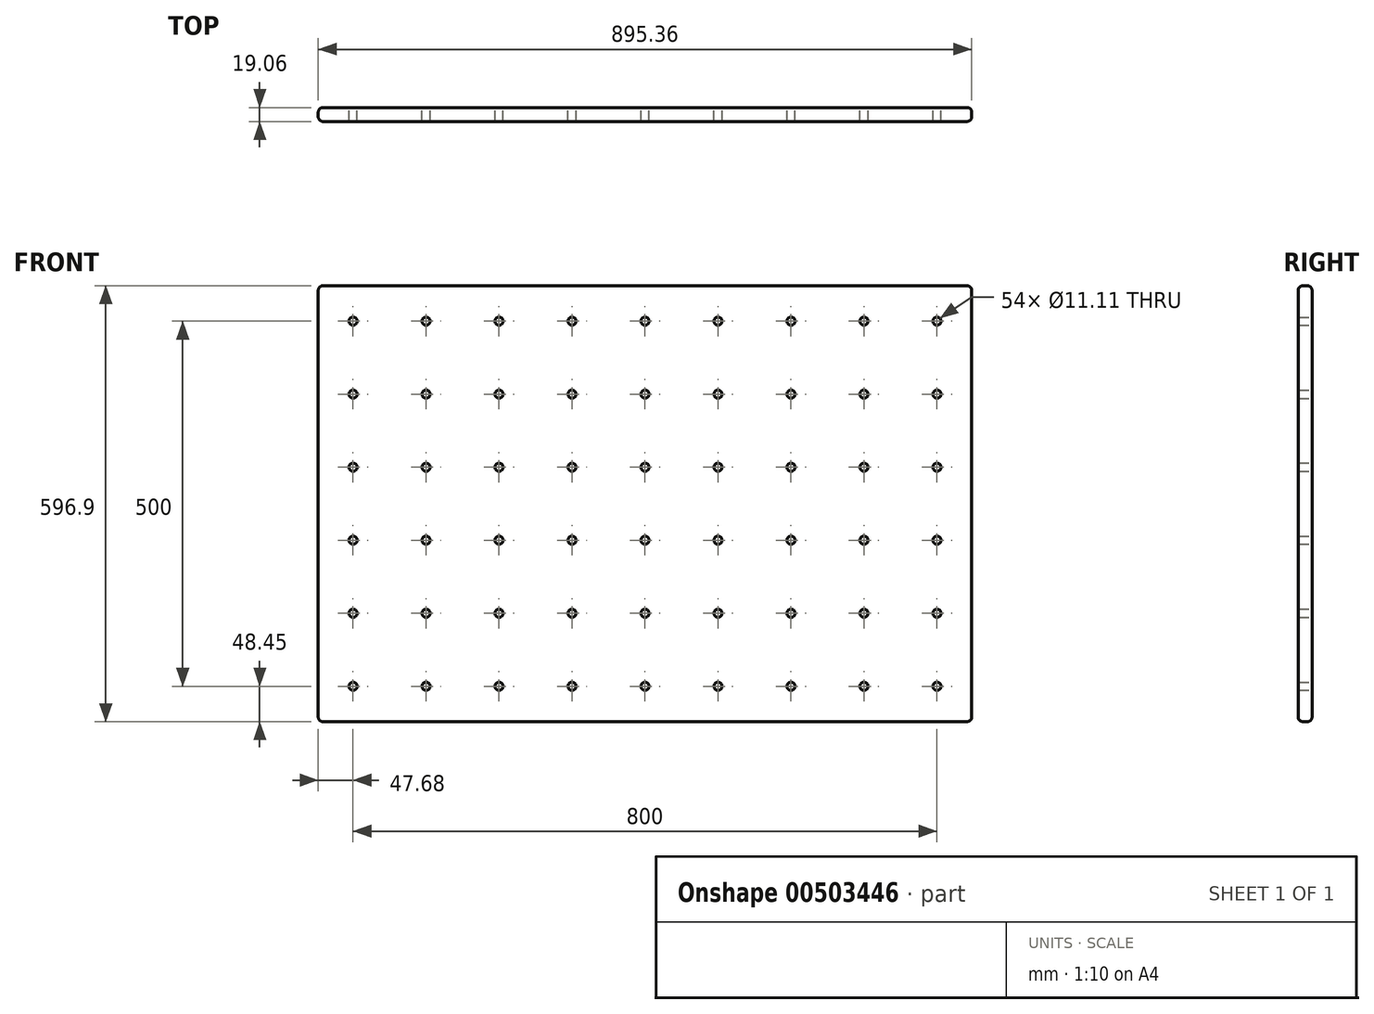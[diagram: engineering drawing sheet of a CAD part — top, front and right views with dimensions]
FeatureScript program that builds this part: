
annotation { "Feature Type Name" : "Feature", "Feature Type Description" : "" }
export const myFeature = defineFeature(function(context is Context, id is Id, definition is map)
    precondition{}
    {
        {
            var Q0;
            Q0=qCreatedBy(makeId("Front.planeOp"),FACE);
            var sketch = newSketch(context, id + "F0", { "sketchPlane" : qUnion([Q0])});
            skLineSegment(sketch, "E0.bottom", {"start": v(-447.68, 298.45) * mm, "end": v(447.68, 298.45) * mm});
            skLineSegment(sketch, "E0.top", {"start": v(-447.68, -298.45) * mm, "end": v(447.67, -298.45) * mm});
            skLineSegment(sketch, "E0.left", {"start": v(-447.68, 298.45) * mm, "end": v(-447.68, -298.45) * mm});
            skLineSegment(sketch, "E0.right", {"start": v(447.68, 298.45) * mm, "end": v(447.67, -298.45) * mm});
            skCircle(sketch, "E1", {"center": v(400, -250) * mm, "radius": 5.56 * mm});
            skCircle(sketch, "E2.0.1.0", {"center": v(400, -150) * mm, "radius": 5.56 * mm});
            skCircle(sketch, "E2.0.2.0", {"center": v(400, -50) * mm, "radius": 5.56 * mm});
            skCircle(sketch, "E2.0.3.0", {"center": v(400, 50) * mm, "radius": 5.56 * mm});
            skCircle(sketch, "E2.0.4.0", {"center": v(400, 150) * mm, "radius": 5.56 * mm});
            skCircle(sketch, "E2.0.5.0", {"center": v(400, 250) * mm, "radius": 5.56 * mm});
            skCircle(sketch, "E2.1.0.0", {"center": v(300, -250) * mm, "radius": 5.56 * mm});
            skCircle(sketch, "E2.1.1.0", {"center": v(300, -150) * mm, "radius": 5.56 * mm});
            skCircle(sketch, "E2.1.2.0", {"center": v(300, -50) * mm, "radius": 5.56 * mm});
            skCircle(sketch, "E2.1.3.0", {"center": v(300, 50) * mm, "radius": 5.56 * mm});
            skCircle(sketch, "E2.1.4.0", {"center": v(300, 150) * mm, "radius": 5.56 * mm});
            skCircle(sketch, "E2.1.5.0", {"center": v(300, 250) * mm, "radius": 5.56 * mm});
            skCircle(sketch, "E2.2.0.0", {"center": v(200, -250) * mm, "radius": 5.56 * mm});
            skCircle(sketch, "E2.2.1.0", {"center": v(200, -150) * mm, "radius": 5.56 * mm});
            skCircle(sketch, "E2.2.2.0", {"center": v(200, -50) * mm, "radius": 5.56 * mm});
            skCircle(sketch, "E2.2.3.0", {"center": v(200, 50) * mm, "radius": 5.56 * mm});
            skCircle(sketch, "E2.2.4.0", {"center": v(200, 150) * mm, "radius": 5.56 * mm});
            skCircle(sketch, "E2.2.5.0", {"center": v(200, 250) * mm, "radius": 5.56 * mm});
            skCircle(sketch, "E2.3.0.0", {"center": v(100, -250) * mm, "radius": 5.56 * mm});
            skCircle(sketch, "E2.3.1.0", {"center": v(100, -150) * mm, "radius": 5.56 * mm});
            skCircle(sketch, "E2.3.2.0", {"center": v(100, -50) * mm, "radius": 5.56 * mm});
            skCircle(sketch, "E2.3.3.0", {"center": v(100, 50) * mm, "radius": 5.56 * mm});
            skCircle(sketch, "E2.3.4.0", {"center": v(100, 150) * mm, "radius": 5.56 * mm});
            skCircle(sketch, "E2.3.5.0", {"center": v(100, 250) * mm, "radius": 5.56 * mm});
            skCircle(sketch, "E2.4.0.0", {"center": v(0, -250) * mm, "radius": 5.56 * mm});
            skCircle(sketch, "E2.4.1.0", {"center": v(0, -150) * mm, "radius": 5.56 * mm});
            skCircle(sketch, "E2.4.2.0", {"center": v(0, -50) * mm, "radius": 5.56 * mm});
            skCircle(sketch, "E2.4.3.0", {"center": v(0, 50) * mm, "radius": 5.56 * mm});
            skCircle(sketch, "E2.4.4.0", {"center": v(0, 150) * mm, "radius": 5.56 * mm});
            skCircle(sketch, "E2.4.5.0", {"center": v(0, 250) * mm, "radius": 5.56 * mm});
            skCircle(sketch, "E2.5.0.0", {"center": v(-100, -250) * mm, "radius": 5.56 * mm});
            skCircle(sketch, "E2.5.1.0", {"center": v(-100, -150) * mm, "radius": 5.56 * mm});
            skCircle(sketch, "E2.5.2.0", {"center": v(-100, -50) * mm, "radius": 5.56 * mm});
            skCircle(sketch, "E2.5.3.0", {"center": v(-100, 50) * mm, "radius": 5.56 * mm});
            skCircle(sketch, "E2.5.4.0", {"center": v(-100, 150) * mm, "radius": 5.56 * mm});
            skCircle(sketch, "E2.5.5.0", {"center": v(-100, 250) * mm, "radius": 5.56 * mm});
            skCircle(sketch, "E2.6.0.0", {"center": v(-200, -250) * mm, "radius": 5.56 * mm});
            skCircle(sketch, "E2.6.1.0", {"center": v(-200, -150) * mm, "radius": 5.56 * mm});
            skCircle(sketch, "E2.6.2.0", {"center": v(-200, -50) * mm, "radius": 5.56 * mm});
            skCircle(sketch, "E2.6.3.0", {"center": v(-200, 50) * mm, "radius": 5.56 * mm});
            skCircle(sketch, "E2.6.4.0", {"center": v(-200, 150) * mm, "radius": 5.56 * mm});
            skCircle(sketch, "E2.6.5.0", {"center": v(-200, 250) * mm, "radius": 5.56 * mm});
            skCircle(sketch, "E2.7.0.0", {"center": v(-300, -250) * mm, "radius": 5.56 * mm});
            skCircle(sketch, "E2.7.1.0", {"center": v(-300, -150) * mm, "radius": 5.56 * mm});
            skCircle(sketch, "E2.7.2.0", {"center": v(-300, -50) * mm, "radius": 5.56 * mm});
            skCircle(sketch, "E2.7.3.0", {"center": v(-300, 50) * mm, "radius": 5.56 * mm});
            skCircle(sketch, "E2.7.4.0", {"center": v(-300, 150) * mm, "radius": 5.56 * mm});
            skCircle(sketch, "E2.7.5.0", {"center": v(-300, 250) * mm, "radius": 5.56 * mm});
            skCircle(sketch, "E2.8.0.0", {"center": v(-400, -250) * mm, "radius": 5.56 * mm});
            skCircle(sketch, "E2.8.1.0", {"center": v(-400, -150) * mm, "radius": 5.56 * mm});
            skCircle(sketch, "E2.8.2.0", {"center": v(-400, -50) * mm, "radius": 5.56 * mm});
            skCircle(sketch, "E2.8.3.0", {"center": v(-400, 50) * mm, "radius": 5.56 * mm});
            skCircle(sketch, "E2.8.4.0", {"center": v(-400, 150) * mm, "radius": 5.56 * mm});
            skCircle(sketch, "E2.8.5.0", {"center": v(-400, 250) * mm, "radius": 5.56 * mm});
            skLineSegment(sketch, "E2.direction1", {"start": v(400, -250) * mm, "end": v(300, -250) * mm, "construction": true});
            skLineSegment(sketch, "E2.direction2", {"start": v(400, -250) * mm, "end": v(400, -150) * mm, "construction": true});
            skSolve(sketch);
        }
        {
            var Q0;
            Q0=makeQuery(id+"F0.imprint","IMPRINT",FACE,{"disambiguationData":[TD([[makeQuery(id+"F0.imprint","IMPRINT",EDGE,{"derivedFrom":sQuery(id+"F0.wireOp",EDGE,"E0.bottom")}),-1.0]])]});
            extrude(context, id + "F1", {"entities" : qUnion([Q0]), "depth" : 19.05 * mm, "symmetric" : true});
        }
        {
            var Q0;
            Q0=makeQuery(id+"F1.opExtrude","SWEPT_EDGE",EDGE,{"disambiguationData":[OSD([sQuery(id+"F0.wireOp",EDGE,"E0.bottom"),sQuery(id+"F0.wireOp",EDGE,"E0.left")])]});
            var Q1;
            Q1=makeQuery(id+"F1.opExtrude","CAP_EDGE",EDGE,{"disambiguationData":[OSD([sQuery(id+"F0.wireOp",EDGE,"E0.bottom")])],"isStart":true});
            var Q2;
            Q2=makeQuery(id+"F1.opExtrude","CAP_EDGE",EDGE,{"disambiguationData":[OSD([sQuery(id+"F0.wireOp",EDGE,"E0.left")])],"isStart":true});
            var Q3;
            Q3=makeQuery(id+"F1.opExtrude","CAP_EDGE",EDGE,{"disambiguationData":[OSD([sQuery(id+"F0.wireOp",EDGE,"E0.left")])],"isStart":false});
            var Q4;
            Q4=makeQuery(id+"F1.opExtrude","SWEPT_EDGE",EDGE,{"disambiguationData":[OSD([sQuery(id+"F0.wireOp",EDGE,"E0.bottom"),sQuery(id+"F0.wireOp",EDGE,"E0.right")])]});
            var Q5;
            Q5=makeQuery(id+"F1.opExtrude","CAP_EDGE",EDGE,{"disambiguationData":[OSD([sQuery(id+"F0.wireOp",EDGE,"E0.bottom")])],"isStart":false});
            var Q6;
            Q6=makeQuery(id+"F1.opExtrude","CAP_EDGE",EDGE,{"disambiguationData":[OSD([sQuery(id+"F0.wireOp",EDGE,"E0.right")])],"isStart":false});
            var Q7;
            Q7=makeQuery(id+"F1.opExtrude","CAP_EDGE",EDGE,{"disambiguationData":[OSD([sQuery(id+"F0.wireOp",EDGE,"E0.top")])],"isStart":false});
            var Q8;
            Q8=makeQuery(id+"F1.opExtrude","SWEPT_EDGE",EDGE,{"disambiguationData":[OSD([sQuery(id+"F0.wireOp",EDGE,"E0.top"),sQuery(id+"F0.wireOp",EDGE,"E0.left")])]});
            var Q9;
            Q9=makeQuery(id+"F1.opExtrude","CAP_EDGE",EDGE,{"disambiguationData":[OSD([sQuery(id+"F0.wireOp",EDGE,"E0.top")])],"isStart":true});
            var Q10;
            Q10=makeQuery(id+"F1.opExtrude","SWEPT_EDGE",EDGE,{"disambiguationData":[OSD([sQuery(id+"F0.wireOp",EDGE,"E0.top"),sQuery(id+"F0.wireOp",EDGE,"E0.right")])]});
            var Q11;
            Q11=makeQuery(id+"F1.opExtrude","CAP_EDGE",EDGE,{"disambiguationData":[OSD([sQuery(id+"F0.wireOp",EDGE,"E0.right")])],"isStart":true});
            fillet(context, id + "F2", {"entities" : qUnion([Q0, Q1, Q2, Q3, Q4, Q5, Q6, Q7, Q8, Q9, Q10, Q11]), "radius" : 6.35 * mm, "tangentPropagation" : true, "allowEdgeOverflow" : false});
        }
        {
            var Q0;
            Q0=makeQuery(id+"F1.opExtrude","CAP_FACE",FACE,{"disambiguationData":[OSD([sQuery(id+"F0.wireOp",EDGE,"E0.bottom"),sQuery(id+"F0.wireOp",EDGE,"E0.top"),sQuery(id+"F0.wireOp",EDGE,"E0.left"),sQuery(id+"F0.wireOp",EDGE,"E0.right"),sQuery(id+"F0.wireOp",EDGE,"E1"),sQuery(id+"F0.wireOp",EDGE,"E2.0.1.0"),sQuery(id+"F0.wireOp",EDGE,"E2.0.2.0"),sQuery(id+"F0.wireOp",EDGE,"E2.0.3.0"),sQuery(id+"F0.wireOp",EDGE,"E2.0.4.0"),sQuery(id+"F0.wireOp",EDGE,"E2.0.5.0"),sQuery(id+"F0.wireOp",EDGE,"E2.1.0.0"),sQuery(id+"F0.wireOp",EDGE,"E2.1.1.0"),sQuery(id+"F0.wireOp",EDGE,"E2.1.2.0"),sQuery(id+"F0.wireOp",EDGE,"E2.1.3.0"),sQuery(id+"F0.wireOp",EDGE,"E2.1.4.0"),sQuery(id+"F0.wireOp",EDGE,"E2.1.5.0"),sQuery(id+"F0.wireOp",EDGE,"E2.2.0.0"),sQuery(id+"F0.wireOp",EDGE,"E2.2.1.0"),sQuery(id+"F0.wireOp",EDGE,"E2.2.2.0"),sQuery(id+"F0.wireOp",EDGE,"E2.2.3.0"),sQuery(id+"F0.wireOp",EDGE,"E2.2.4.0"),sQuery(id+"F0.wireOp",EDGE,"E2.2.5.0"),sQuery(id+"F0.wireOp",EDGE,"E2.3.0.0"),sQuery(id+"F0.wireOp",EDGE,"E2.3.1.0"),sQuery(id+"F0.wireOp",EDGE,"E2.3.2.0"),sQuery(id+"F0.wireOp",EDGE,"E2.3.3.0"),sQuery(id+"F0.wireOp",EDGE,"E2.3.4.0"),sQuery(id+"F0.wireOp",EDGE,"E2.3.5.0"),sQuery(id+"F0.wireOp",EDGE,"E2.4.0.0"),sQuery(id+"F0.wireOp",EDGE,"E2.4.1.0"),sQuery(id+"F0.wireOp",EDGE,"E2.4.2.0"),sQuery(id+"F0.wireOp",EDGE,"E2.4.3.0"),sQuery(id+"F0.wireOp",EDGE,"E2.4.4.0"),sQuery(id+"F0.wireOp",EDGE,"E2.4.5.0"),sQuery(id+"F0.wireOp",EDGE,"E2.5.0.0"),sQuery(id+"F0.wireOp",EDGE,"E2.5.1.0"),sQuery(id+"F0.wireOp",EDGE,"E2.5.2.0"),sQuery(id+"F0.wireOp",EDGE,"E2.5.3.0"),sQuery(id+"F0.wireOp",EDGE,"E2.5.4.0"),sQuery(id+"F0.wireOp",EDGE,"E2.5.5.0"),sQuery(id+"F0.wireOp",EDGE,"E2.6.0.0"),sQuery(id+"F0.wireOp",EDGE,"E2.6.1.0"),sQuery(id+"F0.wireOp",EDGE,"E2.6.2.0"),sQuery(id+"F0.wireOp",EDGE,"E2.6.3.0"),sQuery(id+"F0.wireOp",EDGE,"E2.6.4.0"),sQuery(id+"F0.wireOp",EDGE,"E2.6.5.0"),sQuery(id+"F0.wireOp",EDGE,"E2.7.0.0"),sQuery(id+"F0.wireOp",EDGE,"E2.7.1.0"),sQuery(id+"F0.wireOp",EDGE,"E2.7.2.0"),sQuery(id+"F0.wireOp",EDGE,"E2.7.3.0"),sQuery(id+"F0.wireOp",EDGE,"E2.7.4.0"),sQuery(id+"F0.wireOp",EDGE,"E2.7.5.0"),sQuery(id+"F0.wireOp",EDGE,"E2.8.0.0"),sQuery(id+"F0.wireOp",EDGE,"E2.8.1.0"),sQuery(id+"F0.wireOp",EDGE,"E2.8.2.0"),sQuery(id+"F0.wireOp",EDGE,"E2.8.3.0"),sQuery(id+"F0.wireOp",EDGE,"E2.8.4.0"),sQuery(id+"F0.wireOp",EDGE,"E2.8.5.0")])],"isStart":false});
            var sketch = newSketch(context, id + "F3", { "sketchPlane" : qUnion([Q0])});
            skLineSegment(sketch, "E3", {"start": v(-400.05, 200) * mm, "end": v(0, 200) * mm});
            skLineSegment(sketch, "E4.MirrorCS", {"start": v(400.05, 200) * mm, "end": v(0, 200) * mm});
            skLineSegment(sketch, "E5", {"start": v(-400.05, 200) * mm, "end": v(-400.05, 213.59) * mm});
            skLineSegment(sketch, "E6", {"start": v(-400.05, 200) * mm, "end": v(-404.39, 200) * mm});
            skSolve(sketch);
        }
    });
